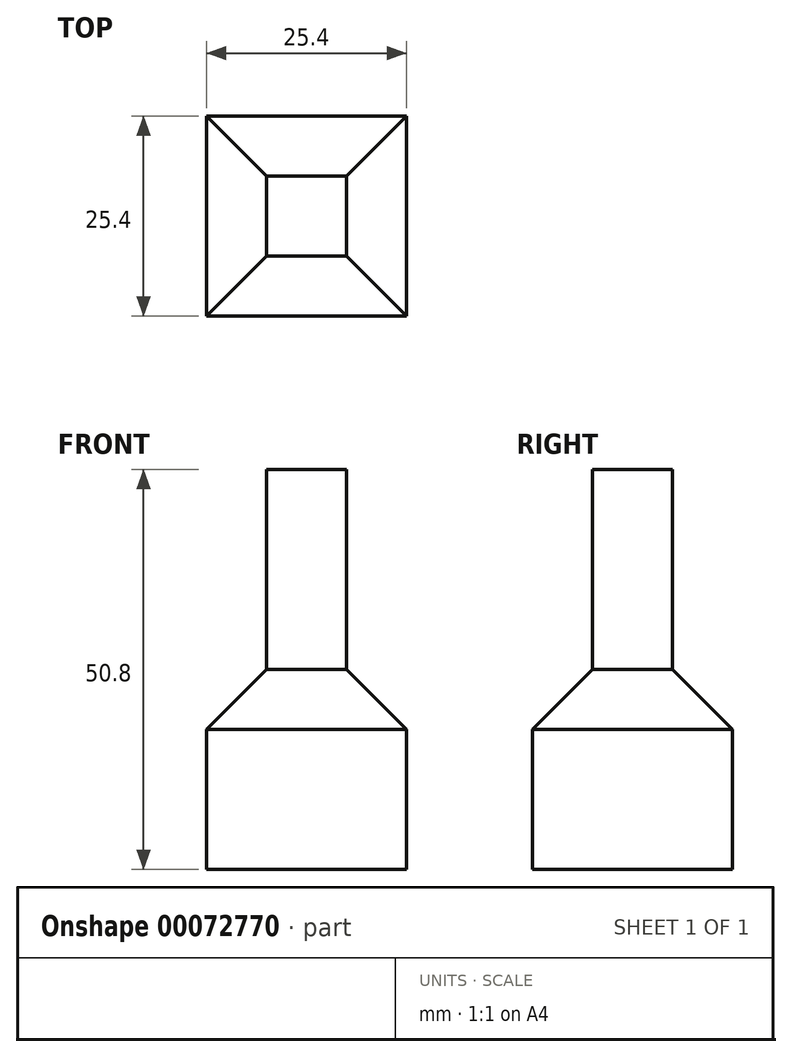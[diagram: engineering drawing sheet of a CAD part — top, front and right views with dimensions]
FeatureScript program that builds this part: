
annotation { "Feature Type Name" : "Feature", "Feature Type Description" : "" }
export const myFeature = defineFeature(function(context is Context, id is Id, definition is map)
    precondition{}
    {
        {
            var Q0;
            Q0=qCreatedBy(makeId("Top.planeOp"),FACE);
            var sketch = newSketch(context, id + "F0", { "sketchPlane" : qUnion([Q0])});
            skLineSegment(sketch, "E0.bottom", {"start": v(0, 0) * mm, "end": v(-25.4, 0) * mm});
            skLineSegment(sketch, "E0.top", {"start": v(0, -25.4) * mm, "end": v(-25.4, -25.4) * mm});
            skLineSegment(sketch, "E0.left", {"start": v(0, 0) * mm, "end": v(0, -25.4) * mm});
            skLineSegment(sketch, "E0.right", {"start": v(-25.4, 0) * mm, "end": v(-25.4, -25.4) * mm});
            skSolve(sketch);
        }
        {
            var Q0;
            Q0 = qSketchRegion(id + "F0", true);
            extrude(context, id + "F1", {"entities" : qUnion([Q0]), "depth" : 25.4 * mm});
        }
        {
            var Q0;
            Q0=makeQuery(id+"F1.opExtrude","CAP_EDGE",EDGE,{"disambiguationData":[OSD([sQuery(id+"F0.wireOp",EDGE,"E0.top")])],"isStart":false});
            var Q1;
            Q1=makeQuery(id+"F1.opExtrude","CAP_EDGE",EDGE,{"disambiguationData":[OSD([sQuery(id+"F0.wireOp",EDGE,"E0.right")])],"isStart":false});
            var Q2;
            Q2=makeQuery(id+"F1.opExtrude","CAP_EDGE",EDGE,{"disambiguationData":[OSD([sQuery(id+"F0.wireOp",EDGE,"E0.bottom")])],"isStart":false});
            var Q3;
            Q3=makeQuery(id+"F1.opExtrude","CAP_EDGE",EDGE,{"disambiguationData":[OSD([sQuery(id+"F0.wireOp",EDGE,"E0.left")])],"isStart":false});
            chamfer(context, id + "F2", {"entities" : qUnion([Q0, Q1, Q2, Q3]), "width" : 7.62 * mm, "tangentPropagation" : true});
        }
        {
            var Q0;
            Q0=makeQuery(id+"F1.opExtrude","CAP_FACE",FACE,{"disambiguationData":[OSD([sQuery(id+"F0.wireOp",EDGE,"E0.bottom"),sQuery(id+"F0.wireOp",EDGE,"E0.top"),sQuery(id+"F0.wireOp",EDGE,"E0.left"),sQuery(id+"F0.wireOp",EDGE,"E0.right")])],"isStart":false});
            var sketch = newSketch(context, id + "F3", { "sketchPlane" : qUnion([Q0])});
            skLineSegment(sketch, "E1.bottom", {"start": v(-17.78, -7.62) * mm, "end": v(-7.62, -7.62) * mm});
            skLineSegment(sketch, "E1.top", {"start": v(-17.78, -17.78) * mm, "end": v(-7.62, -17.78) * mm});
            skLineSegment(sketch, "E1.left", {"start": v(-17.78, -7.62) * mm, "end": v(-17.78, -17.78) * mm});
            skLineSegment(sketch, "E1.right", {"start": v(-7.62, -7.62) * mm, "end": v(-7.62, -17.78) * mm});
            skSolve(sketch);
        }
        {
            var Q0;
            Q0 = qSketchRegion(id + "F3", true);
            extrude(context, id + "F4", {"entities" : qUnion([Q0]), "operationType" : NewBodyOperationType.ADD, "depth" : 25.4 * mm});
        }
    });
